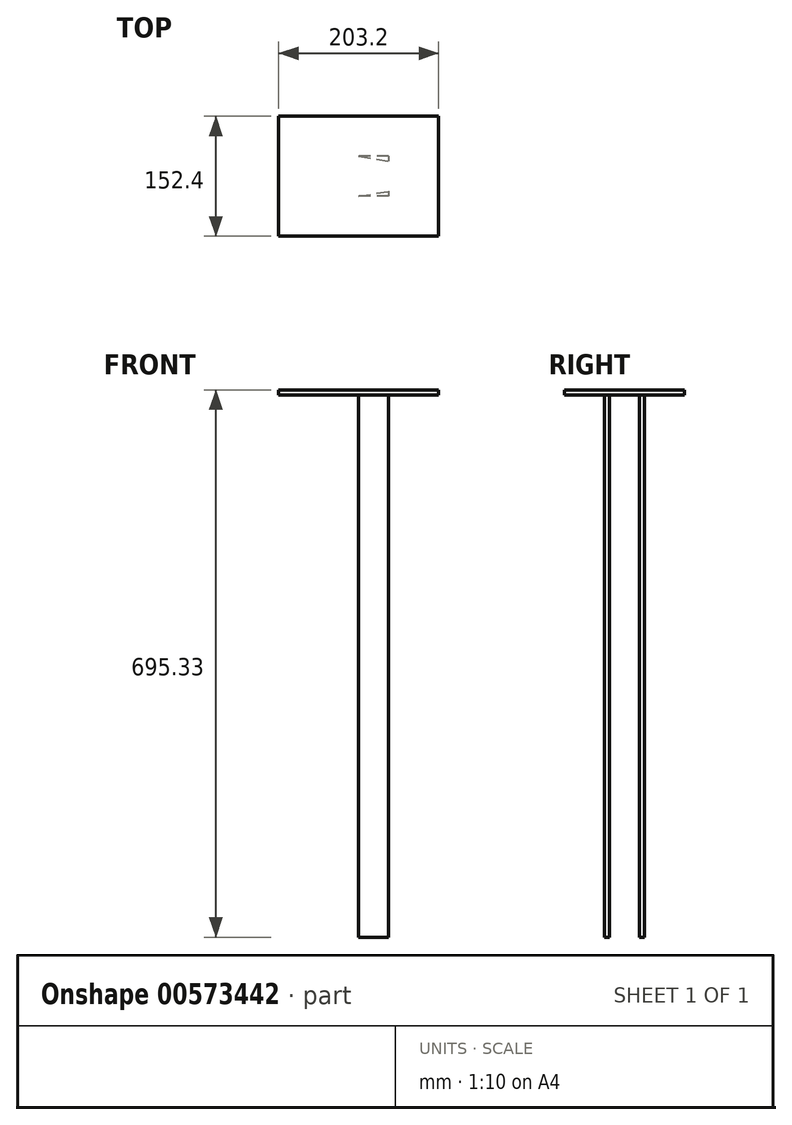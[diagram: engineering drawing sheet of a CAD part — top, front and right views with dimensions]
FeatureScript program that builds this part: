
annotation { "Feature Type Name" : "Feature", "Feature Type Description" : "" }
export const myFeature = defineFeature(function(context is Context, id is Id, definition is map)
    precondition{}
    {
        {
            var Q0;
            Q0=qCreatedBy(makeId("Top.planeOp"),FACE);
            var sketch = newSketch(context, id + "F0", { "sketchPlane" : qUnion([Q0])});
            skLineSegment(sketch, "E0.bottom", {"start": v(38.1, 25.4) * mm, "end": v(-38.1, 25.4) * mm});
            skLineSegment(sketch, "E0.top", {"start": v(38.1, -25.4) * mm, "end": v(-38.1, -25.4) * mm});
            skLineSegment(sketch, "E0.left", {"start": v(38.1, 25.4) * mm, "end": v(38.1, -25.4) * mm});
            skLineSegment(sketch, "E0.right", {"start": v(-38.1, 25.4) * mm, "end": v(-38.1, -25.4) * mm});
            skPoint(sketch, "E0.middle", {"position": v(0, 0) * mm});
            skLineSegment(sketch, "E1", {"start": v(38.1, -25.4) * mm, "end": v(38.1, -19.05) * mm});
            skLineSegment(sketch, "E2", {"start": v(-38.1, -25.4) * mm, "end": v(-38.1, -19.05) * mm});
            skLineSegment(sketch, "E3", {"start": v(-38.1, 25.4) * mm, "end": v(-38.1, 19.05) * mm});
            skLineSegment(sketch, "E4", {"start": v(38.1, 25.4) * mm, "end": v(38.1, 19.05) * mm});
            skLineSegment(sketch, "E5", {"start": v(-38.1, 19.05) * mm, "end": v(0, 25.4) * mm});
            skLineSegment(sketch, "E6", {"start": v(0, 25.4) * mm, "end": v(38.1, 19.05) * mm});
            skLineSegment(sketch, "E7", {"start": v(-38.1, -19.05) * mm, "end": v(0, -25.4) * mm});
            skLineSegment(sketch, "E8", {"start": v(0, -25.4) * mm, "end": v(38.1, -19.05) * mm});
            skSolve(sketch);
        }
        {
            var Q0;
            Q0=makeQuery(id+"F0.imprint","IMPRINT",FACE,{"disambiguationData":[TD([[makeQuery(id+"F0.imprint","IMPRINT",EDGE,{"derivedFrom":sQuery(id+"F0.wireOp",EDGE,"E0.left")}),-1.0]])]});
            extrude(context, id + "F1", {"entities" : qUnion([Q0]), "depth" : 692.15 * mm, "offsetDistance" : 25.4 * mm});
        }
        {
            var Q0;
            Q0=makeQuery(id+"F1.opExtrude","CAP_FACE",FACE,{"disambiguationData":[OSD([sQuery(id+"F0.wireOp",EDGE,"E0.left"),sQuery(id+"F0.wireOp",EDGE,"E0.right"),sQuery(id+"F0.wireOp",EDGE,"E5"),sQuery(id+"F0.wireOp",EDGE,"E6"),sQuery(id+"F0.wireOp",EDGE,"E7"),sQuery(id+"F0.wireOp",EDGE,"E8")])],"isStart":false});
            var sketch = newSketch(context, id + "F2", { "sketchPlane" : qUnion([Q0])});
            skLineSegment(sketch, "E9.bottom", {"start": v(101.6, 76.2) * mm, "end": v(-101.6, 76.2) * mm});
            skLineSegment(sketch, "E9.top", {"start": v(101.6, -76.2) * mm, "end": v(-101.6, -76.2) * mm});
            skLineSegment(sketch, "E9.left", {"start": v(101.6, 76.2) * mm, "end": v(101.6, -76.2) * mm});
            skLineSegment(sketch, "E9.right", {"start": v(-101.6, 76.2) * mm, "end": v(-101.6, -76.2) * mm});
            skPoint(sketch, "E9.middle", {"position": v(0, 0) * mm});
            skSolve(sketch);
        }
        {
            var Q0;
            Q0=makeQuery(id+"F2.imprint","IMPRINT",FACE,{"disambiguationData":[TD([[makeQuery(id+"F2.imprint","IMPRINT",EDGE,{"derivedFrom":sQuery(id+"F2.wireOp",EDGE,"E9.bottom")}),1.0]])]});
            var Q1;
            Q1=makeQuery(id+"F2.imprint","IMPRINT",FACE,{"disambiguationData":[TD([[makeQuery(id+"F2.imprint","IMPRINT",EDGE,{"derivedFrom":makeQuery(id+"F1.opExtrude","CAP_EDGE",EDGE,{"disambiguationData":[OSD([sQuery(id+"F0.wireOp",EDGE,"E0.left")])],"isStart":false})}),-1.0]])]});
            extrude(context, id + "F3", {"entities" : qUnion([Q0, Q1]), "operationType" : NewBodyOperationType.ADD, "depth" : 6.35 * mm, "offsetDistance" : 25.4 * mm});
        }
        {
            var Q0;
            Q0=makeQuery(id+"F1.opExtrude","CAP_FACE",FACE,{"disambiguationData":[OSD([sQuery(id+"F0.wireOp",EDGE,"E0.left"),sQuery(id+"F0.wireOp",EDGE,"E0.right"),sQuery(id+"F0.wireOp",EDGE,"E5"),sQuery(id+"F0.wireOp",EDGE,"E6"),sQuery(id+"F0.wireOp",EDGE,"E7"),sQuery(id+"F0.wireOp",EDGE,"E8")])],"isStart":true});
            extrude(context, id + "F4", {"entities" : qUnion([Q0]), "operationType" : NewBodyOperationType.REMOVE, "oppositeDirection" : true, "depth" : 3.17 * mm, "offsetDistance" : 25.4 * mm});
        }
    });
